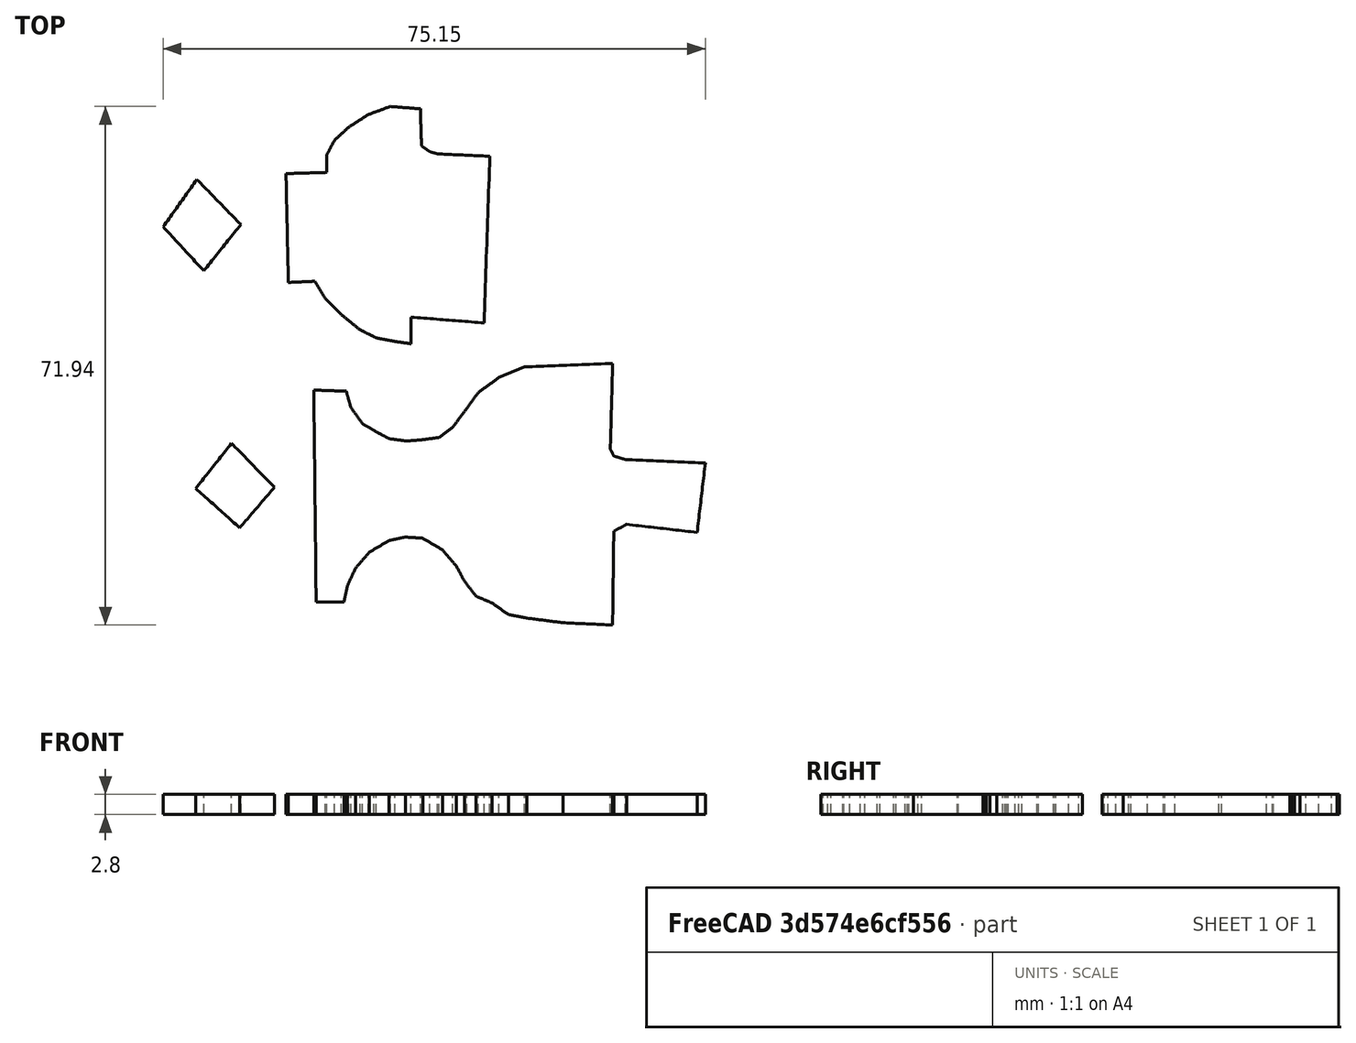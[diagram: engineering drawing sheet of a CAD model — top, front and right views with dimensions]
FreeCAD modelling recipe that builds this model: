
FCSTD DOCUMENT  (FreeCAD 0.15R3874 (Git))
Label: face
License: CC-BY 3.0
LicenseURL: http://creativecommons.org/licenses/by/3.0/
objects: Part::Feature×4, Part::Extrusion×4
note: 8 computed .brp shape members not serialized (recipe doc carries the construction recipe); baked Part::Feature solids carry a one-line shape summary decoded from their .brp

FEATURE [Part::Feature] path6390
  shape: bbox 10.76 x 12.69 x 2e-07 mm, 1 faces, 0 solids (baked)
FEATURE [Part::Feature] path6392
  shape: bbox 10.92 x 11.72 x 2e-07 mm, 1 faces, 0 solids (baked)
FEATURE [Part::Feature] path7001
  shape: bbox 28.26 x 32.92 x 2e-07 mm, 1 faces, 0 solids (baked)
FEATURE [Part::Feature] path7003
  shape: bbox 54.28 x 36.29 x 2e-07 mm, 1 faces, 0 solids (baked)
FEATURE [Part::Extrusion] Extrude
  Base = -> path7001
  Dir = (0,0,2.8)
  Solid = false
FEATURE [Part::Extrusion] Extrude001
  Base = -> path6390
  Dir = (0,0,2.8)
  Solid = false
FEATURE [Part::Extrusion] Extrude002
  Base = -> path7003
  Dir = (0,0,2.8)
  Solid = false
FEATURE [Part::Extrusion] Extrude003
  Base = -> path6392
  Dir = (0,0,2.8)
  Solid = false
